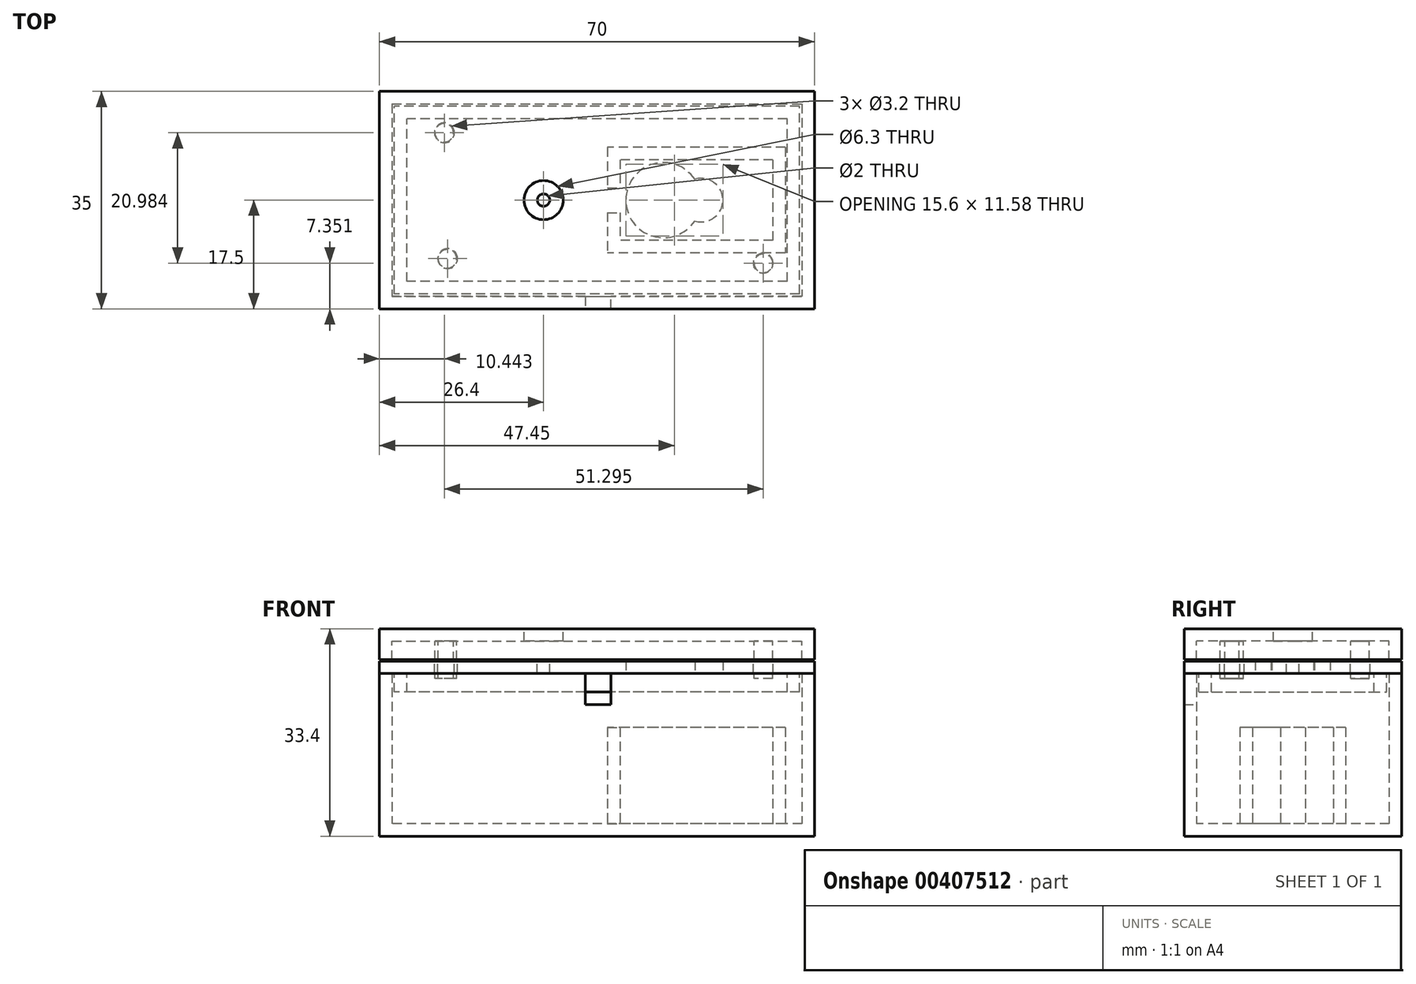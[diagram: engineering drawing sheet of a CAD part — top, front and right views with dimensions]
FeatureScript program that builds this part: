
annotation { "Feature Type Name" : "Feature", "Feature Type Description" : "" }
export const myFeature = defineFeature(function(context is Context, id is Id, definition is map)
    precondition{}
    {
        {
            var Q0;
            Q0=qCreatedBy(makeId("Top.planeOp"),FACE);
            var sketch = newSketch(context, id + "F0", { "sketchPlane" : qUnion([Q0])});
            skLineSegment(sketch, "E0.bottom", {"start": v(35, 17.5) * mm, "end": v(-35, 17.5) * mm});
            skLineSegment(sketch, "E0.top", {"start": v(35, -17.5) * mm, "end": v(-35, -17.5) * mm});
            skLineSegment(sketch, "E0.left", {"start": v(35, 17.5) * mm, "end": v(35, -17.5) * mm});
            skLineSegment(sketch, "E0.right", {"start": v(-35, 17.5) * mm, "end": v(-35, -17.5) * mm});
            skPoint(sketch, "E0.middle", {"position": v(0, 0) * mm});
            skLineSegment(sketch, "E1", {"start": v(-43.34, 0) * mm, "end": v(44.04, 0) * mm, "construction": true});
            skPoint(sketch, "E1.startSnap0", {"position": v(-35, 0) * mm});
            skPoint(sketch, "E1.endSnap0", {"position": v(-35, 0) * mm});
            skLineSegment(sketch, "E2", {"start": v(0, 25.29) * mm, "end": v(0, -30.37) * mm, "construction": true});
            skPoint(sketch, "E2.startSnap0", {"position": v(0, 17.5) * mm});
            skLineSegment(sketch, "E3", {"start": v(17.5, 25.15) * mm, "end": v(17.5, -26.82) * mm, "construction": true});
            skSolve(sketch);
        }
        {
            var Q0;
            Q0=makeQuery(id+"F0.imprint","IMPRINT",FACE,{"disambiguationData":[TD([[makeQuery(id+"F0.imprint","IMPRINT",EDGE,{"derivedFrom":sQuery(id+"F0.wireOp",EDGE,"E0.bottom")}),1.0]])]});
            extrude(context, id + "F1", {"entities" : qUnion([Q0]), "depth" : 2 * mm});
        }
        {
            var Q0;
            Q0=makeQuery(id+"F1.opExtrude","CAP_FACE",FACE,{"disambiguationData":[OSD([sQuery(id+"F0.wireOp",EDGE,"E0.bottom"),sQuery(id+"F0.wireOp",EDGE,"E0.top"),sQuery(id+"F0.wireOp",EDGE,"E0.left"),sQuery(id+"F0.wireOp",EDGE,"E0.right")])],"isStart":false});
            var sketch = newSketch(context, id + "F2", { "sketchPlane" : qUnion([Q0])});
            skLineSegment(sketch, "E4.bottom", {"start": v(33, 15.5) * mm, "end": v(-33, 15.5) * mm});
            skLineSegment(sketch, "E4.top", {"start": v(33, -15.5) * mm, "end": v(-33, -15.5) * mm});
            skLineSegment(sketch, "E4.left", {"start": v(33, 15.5) * mm, "end": v(33, -15.5) * mm});
            skLineSegment(sketch, "E4.right", {"start": v(-33, 15.5) * mm, "end": v(-33, -15.5) * mm});
            skPoint(sketch, "E4.middle", {"position": v(0, 0) * mm});
            skSolve(sketch);
        }
        {
            var Q0;
            Q0=makeQuery(id+"F2.imprint","IMPRINT",FACE,{"disambiguationData":[TD([[makeQuery(id+"F2.imprint","IMPRINT",EDGE,{"derivedFrom":sQuery(id+"F2.wireOp",EDGE,"E4.bottom")}),-1.0]])]});
            extrude(context, id + "F3", {"entities" : qUnion([Q0]), "operationType" : NewBodyOperationType.ADD, "depth" : 24.2 * mm});
        }
        {
            var Q0;
            Q0=makeQuery(id+"F1.opExtrude","CAP_FACE",FACE,{"disambiguationData":[OSD([sQuery(id+"F0.wireOp",EDGE,"E0.bottom"),sQuery(id+"F0.wireOp",EDGE,"E0.top"),sQuery(id+"F0.wireOp",EDGE,"E0.left"),sQuery(id+"F0.wireOp",EDGE,"E0.right")])],"isStart":false});
            var sketch = newSketch(context, id + "F4", { "sketchPlane" : qUnion([Q0])});
            skPoint(sketch, "E5.endSnap0", {"position": v(33, 0) * mm});
            skLineSegment(sketch, "E6", {"start": v(16, 6.58) * mm, "end": v(16, -8.68) * mm, "construction": true});
            skLineSegment(sketch, "E7.bottom", {"start": v(28.3, 6.5) * mm, "end": v(3.7, 6.5) * mm});
            skLineSegment(sketch, "E7.top", {"start": v(28.3, -6.5) * mm, "end": v(3.7, -6.5) * mm});
            skLineSegment(sketch, "E7.left", {"start": v(28.3, 6.5) * mm, "end": v(28.3, -6.5) * mm});
            skLineSegment(sketch, "E7.right", {"start": v(3.7, 6.5) * mm, "end": v(3.7, -6.5) * mm});
            skPoint(sketch, "E7.middle", {"position": v(16, 0) * mm});
            skLineSegment(sketch, "E8.bottom", {"start": v(30.3, 8.5) * mm, "end": v(1.7, 8.5) * mm});
            skLineSegment(sketch, "E8.top", {"start": v(30.3, -8.5) * mm, "end": v(1.7, -8.5) * mm});
            skLineSegment(sketch, "E8.left", {"start": v(30.3, 8.5) * mm, "end": v(30.3, -8.5) * mm});
            skLineSegment(sketch, "E8.right", {"start": v(1.7, 8.5) * mm, "end": v(1.7, -8.5) * mm});
            skLineSegment(sketch, "E9", {"start": v(1.7, 2) * mm, "end": v(3.7, 2) * mm});
            skLineSegment(sketch, "E10", {"start": v(0, 13.02) * mm, "end": v(0, -13.76) * mm, "construction": true});
            skLineSegment(sketch, "E11", {"start": v(0, 0) * mm, "end": v(16, 0) * mm, "construction": true});
            skLineSegment(sketch, "E12", {"start": v(1.7, -2) * mm, "end": v(3.7, -2) * mm});
            skSolve(sketch);
        }
        {
            var Q0;
            {var subQ7=sQuery(id+"F4.wireOp",EDGE,"E7.bottom");Q0=makeQuery(id+"F4.imprint","IMPRINT",FACE,{"disambiguationData":[TD([[makeQuery(id+"F4.imprint","IMPRINT",EDGE,{"derivedFrom":subQ7}),-1.0]])]});}
            extrude(context, id + "F5", {"entities" : qUnion([Q0]), "operationType" : NewBodyOperationType.ADD, "depth" : 15.5 * mm});
        }
        {
            var Q0;
            Q0=makeQuery(id+"F3.opExtrude","CAP_FACE",FACE,{"disambiguationData":[OSD([sQuery(id+"F0.wireOp",EDGE,"E0.bottom"),sQuery(id+"F0.wireOp",EDGE,"E0.top"),sQuery(id+"F0.wireOp",EDGE,"E0.left"),sQuery(id+"F0.wireOp",EDGE,"E0.right"),sQuery(id+"F2.wireOp",EDGE,"E4.bottom"),sQuery(id+"F2.wireOp",EDGE,"E4.top"),sQuery(id+"F2.wireOp",EDGE,"E4.left"),sQuery(id+"F2.wireOp",EDGE,"E4.right")])],"isStart":false});
            var sketch = newSketch(context, id + "F6", { "sketchPlane" : qUnion([Q0])});
            skLineSegment(sketch, "E13.bottom", {"start": v(-35, 17.5) * mm, "end": v(35, 17.5) * mm});
            skLineSegment(sketch, "E13.top", {"start": v(-35, -17.5) * mm, "end": v(35, -17.5) * mm});
            skLineSegment(sketch, "E13.left", {"start": v(-35, 17.5) * mm, "end": v(-35, -17.5) * mm});
            skLineSegment(sketch, "E13.right", {"start": v(35, 17.5) * mm, "end": v(35, -17.5) * mm});
            skPoint(sketch, "E13.middle", {"position": v(0, 0) * mm});
            skSolve(sketch);
        }
        {
            var Q0;
            Q0 = qSketchRegion(id + "F6", true);
            extrude(context, id + "F7", {"entities" : qUnion([Q0]), "depth" : 2 * mm});
        }
        {
            var Q0;
            Q0=makeQuery(id+"F7.opExtrude","CAP_FACE",FACE,{"disambiguationData":[OSD([sQuery(id+"F6.wireOp",EDGE,"E13.bottom"),sQuery(id+"F6.wireOp",EDGE,"E13.top"),sQuery(id+"F6.wireOp",EDGE,"E13.left"),sQuery(id+"F6.wireOp",EDGE,"E13.right")])],"isStart":true});
            var sketch = newSketch(context, id + "F8", { "sketchPlane" : qUnion([Q0])});
            skPoint(sketch, "E14.middle", {"position": v(0, 0) * mm});
            skLineSegment(sketch, "E15.bottom", {"start": v(32.6, 15.1) * mm, "end": v(-32.6, 15.1) * mm});
            skLineSegment(sketch, "E15.top", {"start": v(32.6, -15.1) * mm, "end": v(-32.6, -15.1) * mm});
            skLineSegment(sketch, "E15.left", {"start": v(32.6, 15.1) * mm, "end": v(32.6, -15.1) * mm});
            skLineSegment(sketch, "E15.right", {"start": v(-32.6, 15.1) * mm, "end": v(-32.6, -15.1) * mm});
            skLineSegment(sketch, "E16.bottom", {"start": v(30.6, 13.1) * mm, "end": v(-30.6, 13.1) * mm});
            skLineSegment(sketch, "E16.top", {"start": v(30.6, -13.1) * mm, "end": v(-30.6, -13.1) * mm});
            skLineSegment(sketch, "E16.left", {"start": v(30.6, 13.1) * mm, "end": v(30.6, -13.1) * mm});
            skLineSegment(sketch, "E16.right", {"start": v(-30.6, 13.1) * mm, "end": v(-30.6, -13.1) * mm});
            skSolve(sketch);
        }
        {
            var Q0;
            Q0 = qSketchRegion(id + "F8", true);
            extrude(context, id + "F9", {"entities" : qUnion([Q0]), "operationType" : NewBodyOperationType.ADD, "depth" : 3 * mm});
        }
        {
            var Q0;
            Q0=makeQuery(id+"F9.boolean.opBoolean","SPLIT",FACE,{"disambiguationData":[TD([makeQuery(id+"F9.opExtrude","SWEPT_FACE",FACE,{"disambiguationData":[OSD([sQuery(id+"F8.wireOp",EDGE,"E16.bottom")])]})])],"derivedFrom":makeQuery(id+"F7.opExtrude","CAP_FACE",FACE,{"disambiguationData":[OSD([sQuery(id+"F6.wireOp",EDGE,"E13.bottom"),sQuery(id+"F6.wireOp",EDGE,"E13.top"),sQuery(id+"F6.wireOp",EDGE,"E13.left"),sQuery(id+"F6.wireOp",EDGE,"E13.right")])],"isStart":true})});
            var sketch = newSketch(context, id + "F10", { "sketchPlane" : qUnion([Q0])});
            skLineSegment(sketch, "E17", {"start": v(0, 0) * mm, "end": v(39.34, 0) * mm, "construction": true});
            skPoint(sketch, "E17.endSnap0", {"position": v(30.6, 0) * mm});
            skLineSegment(sketch, "E18", {"start": v(16, 10.66) * mm, "end": v(16, -23.3) * mm, "construction": true});
            skLineSegment(sketch, "E19", {"start": v(10.7, 5.78) * mm, "end": v(10.7, -5.4) * mm, "construction": true});
            skCircle(sketch, "E20", {"center": v(10.7, 0) * mm, "radius": 6.05 * mm});
            skLineSegment(sketch, "E21", {"start": v(0, 0) * mm, "end": v(0, -22.52) * mm, "construction": true});
            skPoint(sketch, "E21.endSnap0", {"position": v(0, -13.1) * mm});
            skLineSegment(sketch, "E22", {"start": v(0, -20.75) * mm, "end": v(16, -20.75) * mm, "construction": true});
            skLineSegment(sketch, "E23", {"start": v(0, -2.34) * mm, "end": v(10.7, -2.34) * mm, "construction": true});
            skLineSegment(sketch, "E24", {"start": v(0, -6.94) * mm, "end": v(16, -6.94) * mm, "construction": true});
            skCircle(sketch, "E25", {"center": v(16.75, 0) * mm, "radius": 3.5 * mm});
            skSolve(sketch);
        }
        {
            var Q0;
            Q0 = qSketchRegion(id + "F10", true);
            extrude(context, id + "F11", {"entities" : qUnion([Q0]), "operationType" : NewBodyOperationType.REMOVE, "oppositeDirection" : true, "depth" : 25 * mm});
        }
        {
            var Q0;
            Q0=makeQuery(id+"F8.imprint","IMPRINT",FACE,{"disambiguationData":[TD([[makeQuery(id+"F8.imprint","IMPRINT",EDGE,{"derivedFrom":sQuery(id+"F8.wireOp",EDGE,"E15.bottom")}),-1.0]])]});
            var sketch = newSketch(context, id + "F12", { "sketchPlane" : qUnion([Q0])});
            skLineSegment(sketch, "E26", {"start": v(-1.9, 15.38) * mm, "end": v(-1.9, 17.71) * mm});
            skLineSegment(sketch, "E27", {"start": v(-1.9, 17.71) * mm, "end": v(2.23, 17.71) * mm});
            skLineSegment(sketch, "E28", {"start": v(2.23, 17.71) * mm, "end": v(2.23, 15.15) * mm});
            skLineSegment(sketch, "E29", {"start": v(2.23, 15.15) * mm, "end": v(-1.9, 15.15) * mm});
            skLineSegment(sketch, "E30", {"start": v(-1.9, 15.15) * mm, "end": v(-1.9, 15.38) * mm});
            skSolve(sketch);
        }
        {
            var Q0;
            Q0 = qSketchRegion(id + "F12", true);
            extrude(context, id + "F13", {"entities" : qUnion([Q0]), "operationType" : NewBodyOperationType.REMOVE, "depth" : 5 * mm});
        }
        {
            var Q0;
            Q0=makeQuery(id+"F7.opExtrude","CAP_FACE",FACE,{"disambiguationData":[OSD([sQuery(id+"F6.wireOp",EDGE,"E13.bottom"),sQuery(id+"F6.wireOp",EDGE,"E13.top"),sQuery(id+"F6.wireOp",EDGE,"E13.left"),sQuery(id+"F6.wireOp",EDGE,"E13.right")])],"isStart":false});
            var sketch = newSketch(context, id + "F14", { "sketchPlane" : qUnion([Q0])});
            skLineSegment(sketch, "E31", {"start": v(10.7, 0) * mm, "end": v(-8.6, 0) * mm, "construction": true});
            skPoint(sketch, "E31.endSnap0", {"position": v(4.65, 0) * mm});
            skCircle(sketch, "E32", {"center": v(-8.6, 0) * mm, "radius": 1 * mm});
            skSolve(sketch);
        }
        {
            var Q0;
            Q0 = qSketchRegion(id + "F14", true);
            extrude(context, id + "F15", {"entities" : qUnion([Q0]), "operationType" : NewBodyOperationType.REMOVE, "oppositeDirection" : true, "depth" : 3 * mm});
        }
        {
            var Q0;
            Q0=makeQuery(id+"F7.opExtrude","CAP_FACE",FACE,{"disambiguationData":[OSD([sQuery(id+"F6.wireOp",EDGE,"E13.bottom"),sQuery(id+"F6.wireOp",EDGE,"E13.top"),sQuery(id+"F6.wireOp",EDGE,"E13.left"),sQuery(id+"F6.wireOp",EDGE,"E13.right")])],"isStart":false});
            var Q1;
            Q1 = qBodyType(qCreatedBy(id + "F21" ,EDGE), BodyType.WIRE);
            cPlane(context, id + "F16", {"entities" : qUnion([Q0, Q1]), "cplaneType" : CPlaneType.OFFSET, "offset" : 3.2 * mm, "width" : 150 * mm, "height" : 150 * mm});
        }
        {
            var Q0;
            Q0=qCreatedBy(id+"F16.planeOp",FACE);
            var sketch = newSketch(context, id + "F17", { "sketchPlane" : qUnion([Q0])});
            skLineSegment(sketch, "E33.bottom", {"start": v(-35, 17.5) * mm, "end": v(35, 17.5) * mm});
            skLineSegment(sketch, "E33.top", {"start": v(-35, -17.5) * mm, "end": v(35, -17.5) * mm});
            skLineSegment(sketch, "E33.left", {"start": v(-35, 17.5) * mm, "end": v(-35, -17.5) * mm});
            skLineSegment(sketch, "E33.right", {"start": v(35, 17.5) * mm, "end": v(35, -17.5) * mm});
            skPoint(sketch, "E33.middle", {"position": v(0, 0) * mm});
            skLineSegment(sketch, "E34.0", {"start": v(-35.19, 17.69) * mm, "end": v(-35.19, -17.69) * mm});
            skLineSegment(sketch, "E34.1", {"start": v(-35.19, 17.69) * mm, "end": v(35.19, 17.69) * mm});
            skLineSegment(sketch, "E34.2", {"start": v(35.19, 17.69) * mm, "end": v(35.19, -17.69) * mm});
            skLineSegment(sketch, "E34.3", {"start": v(-35.19, -17.69) * mm, "end": v(35.19, -17.69) * mm});
            skSolve(sketch);
        }
        {
            var Q0;
            Q0=makeQuery(id+"F17.imprint","IMPRINT",FACE,{"disambiguationData":[TD([[makeQuery(id+"F17.imprint","IMPRINT",EDGE,{"derivedFrom":sQuery(id+"F17.wireOp",EDGE,"E33.bottom")}),-1.0]])]});
            extrude(context, id + "F18", {"entities" : qUnion([Q0]), "depth" : 2 * mm});
        }
        {
            var Q0;
            Q0=qCreatedBy(id+"F16.planeOp",FACE);
            var sketch = newSketch(context, id + "F19", { "sketchPlane" : qUnion([Q0])});
            skLineSegment(sketch, "E35.bottom", {"start": v(-35, 17.5) * mm, "end": v(35, 17.5) * mm});
            skLineSegment(sketch, "E35.top", {"start": v(-35, -17.5) * mm, "end": v(35, -17.5) * mm});
            skLineSegment(sketch, "E35.left", {"start": v(-35, 17.5) * mm, "end": v(-35, -17.5) * mm});
            skLineSegment(sketch, "E35.right", {"start": v(35, 17.5) * mm, "end": v(35, -17.5) * mm});
            skPoint(sketch, "E35.middle", {"position": v(0, 0) * mm});
            skLineSegment(sketch, "E36.bottom", {"start": v(-33, 15.5) * mm, "end": v(33, 15.5) * mm});
            skLineSegment(sketch, "E36.top", {"start": v(-33, -15.5) * mm, "end": v(33, -15.5) * mm});
            skLineSegment(sketch, "E36.left", {"start": v(-33, 15.5) * mm, "end": v(-33, -15.5) * mm});
            skLineSegment(sketch, "E36.right", {"start": v(33, 15.5) * mm, "end": v(33, -15.5) * mm});
            skSolve(sketch);
        }
        {
            var Q0;
            Q0 = qSketchRegion(id + "F19", true);
            extrude(context, id + "F20", {"entities" : qUnion([Q0]), "operationType" : NewBodyOperationType.ADD, "oppositeDirection" : true, "depth" : 3 * mm});
        }
        {
            var Q0;
            Q0=makeQuery(id+"F18.opExtrude","CAP_FACE",FACE,{"disambiguationData":[OSD([sQuery(id+"F17.wireOp",EDGE,"E33.bottom"),sQuery(id+"F17.wireOp",EDGE,"E33.top"),sQuery(id+"F17.wireOp",EDGE,"E33.left"),sQuery(id+"F17.wireOp",EDGE,"E33.right")])],"isStart":false});
            var sketch = newSketch(context, id + "F21", { "sketchPlane" : qUnion([Q0])});
            skCircle(sketch, "E37", {"center": v(-8.6, 0) * mm, "radius": 3.15 * mm});
            skSolve(sketch);
        }
        {
            var Q0;
            Q0 = qSketchRegion(id + "F21", true);
            extrude(context, id + "F22", {"entities" : qUnion([Q0]), "operationType" : NewBodyOperationType.REMOVE, "oppositeDirection" : true, "depth" : 2 * mm});
        }
        {
            var Q0;
            Q0=qCreatedBy(id+"F16.planeOp",FACE);
            var sketch = newSketch(context, id + "F23", { "sketchPlane" : qUnion([Q0])});
            skCircle(sketch, "E38", {"center": v(-24.6, 10.84) * mm, "radius": 1.5 * mm});
            skCircle(sketch, "E39", {"center": v(-24.07, -9.44) * mm, "radius": 1.5 * mm});
            skCircle(sketch, "E40", {"center": v(26.79, -10.17) * mm, "radius": 1.5 * mm});
            skSolve(sketch);
        }
        {
            var Q0;
            Q0 = qSketchRegion(id + "F23", true);
            extrude(context, id + "F24", {"entities" : qUnion([Q0]), "operationType" : NewBodyOperationType.ADD, "oppositeDirection" : true, "depth" : 6 * mm});
        }
        {
            var Q0;
            Q0=makeQuery(id+"F14.imprint","IMPRINT",FACE,{"disambiguationData":[TD([[makeQuery(id+"F14.imprint","IMPRINT",EDGE,{"derivedFrom":sQuery(id+"F14.wireOp",EDGE,"E32")}),-1.0]])]});
            var sketch = newSketch(context, id + "F25", { "sketchPlane" : qUnion([Q0])});
            skCircle(sketch, "E41", {"center": v(-24.56, 10.84) * mm, "radius": 1.6 * mm});
            skCircle(sketch, "E42", {"center": v(-24.03, -9.42) * mm, "radius": 1.6 * mm});
            skCircle(sketch, "E43", {"center": v(26.74, -10.15) * mm, "radius": 1.6 * mm});
            skSolve(sketch);
        }
        {
            var Q0;
            Q0 = qSketchRegion(id + "F25", true);
            extrude(context, id + "F26", {"entities" : qUnion([Q0]), "operationType" : NewBodyOperationType.REMOVE, "oppositeDirection" : true, "depth" : 2 * mm});
        }
    });
